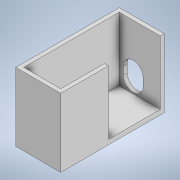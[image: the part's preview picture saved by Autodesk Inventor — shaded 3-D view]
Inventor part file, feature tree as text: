
AUTODESK INVENTOR PART (.ipt)
format: ipt  version: 2020 (Build 240168000, 168)  size: 131,072 bytes
history: native  units: in
note: dims shown in document units (in); Inventor stores cm internally (conversion verified against a paired STEP export)
features: extrude x3, sketch x3, fillet x1
ambient origin geometry x8: Origin, YZ Plane, XZ Plane, XY Plane, X Axis, Y Axis, Z Axis, Center Point
bodies: Solid1 (feature_tree)
feature tree (7):
  extrude  "Extrusion1"  Depth=2.6in
  extrude  "Extrusion2"  Depth=0.1in
  extrude  "Extrusion3"  Depth=0.1in
  fillet  "Fillet1"  Radius=0.1in
  sketch  "Sketch1"  dims[d0=1.13in d1=2.6in]
  sketch  "Sketch2"  dims[d2=0.12in d3=0.0in d4=0.1in]
  sketch  "Sketch3"  dims[d5=0.1in d6=0.1in d7=0.1in d8=1.1in d9=1.6in d10=0.0in d11=0.2in d12=0.15in d13=0.5in d14=0.7in d15=0.1in d16=0.0in d17=0.25in]
